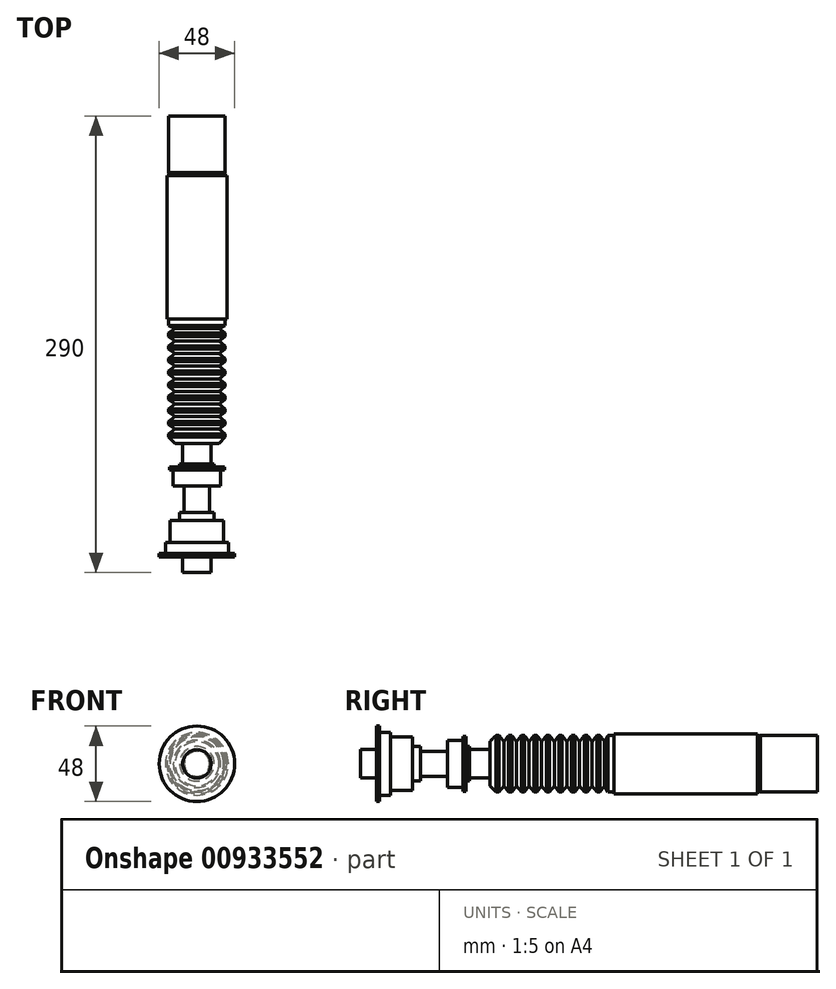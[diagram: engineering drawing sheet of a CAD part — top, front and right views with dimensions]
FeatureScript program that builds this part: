
annotation { "Feature Type Name" : "Feature", "Feature Type Description" : "" }
export const myFeature = defineFeature(function(context is Context, id is Id, definition is map)
    precondition{}
    {
        {
            var Q0;
            Q0=qCreatedBy(makeId("Right.planeOp"),FACE);
            var sketch = newSketch(context, id + "F0", { "sketchPlane" : qUnion([Q0])});
            skLineSegment(sketch, "E0.bottom", {"start": v(0, -9) * mm, "end": v(10, -9) * mm});
            skLineSegment(sketch, "E0.top", {"start": v(0, 9) * mm, "end": v(10, 9) * mm});
            skLineSegment(sketch, "E0.left", {"start": v(0, -9) * mm, "end": v(0, 9) * mm});
            skLineSegment(sketch, "E0.right", {"start": v(10, -9) * mm, "end": v(10, 9) * mm});
            skPoint(sketch, "E0.middle", {"position": v(5, 0) * mm});
            skLineSegment(sketch, "E1.bottom", {"start": v(10, -24) * mm, "end": v(12, -24) * mm});
            skLineSegment(sketch, "E1.top", {"start": v(10, 24) * mm, "end": v(12, 24) * mm});
            skLineSegment(sketch, "E1.left", {"start": v(10, -24) * mm, "end": v(10, 24) * mm});
            skLineSegment(sketch, "E1.right", {"start": v(12, -24) * mm, "end": v(12, 24) * mm});
            skPoint(sketch, "E1.middle", {"position": v(11, 0) * mm});
            skLineSegment(sketch, "E2.bottom", {"start": v(12, -20) * mm, "end": v(19, -20) * mm});
            skLineSegment(sketch, "E2.top", {"start": v(12, 20) * mm, "end": v(19, 20) * mm});
            skLineSegment(sketch, "E2.left", {"start": v(12, -20) * mm, "end": v(12, 20) * mm});
            skLineSegment(sketch, "E2.right", {"start": v(19, -20) * mm, "end": v(19, 20) * mm});
            skPoint(sketch, "E2.middle", {"position": v(15.5, 0) * mm});
            skPoint(sketch, "E2.middle.positionSnap0", {"position": v(12, 0) * mm});
            skPoint(sketch, "E2.centerSnap0", {"position": v(12, 0) * mm});
            skLineSegment(sketch, "E3.bottom", {"start": v(19, -17) * mm, "end": v(33, -17) * mm});
            skLineSegment(sketch, "E3.top", {"start": v(19, 17) * mm, "end": v(33, 17) * mm});
            skLineSegment(sketch, "E3.left", {"start": v(19, -17) * mm, "end": v(19, 17) * mm});
            skLineSegment(sketch, "E3.right", {"start": v(33, -17) * mm, "end": v(33, 17) * mm});
            skPoint(sketch, "E3.middle", {"position": v(26, 0) * mm});
            skLineSegment(sketch, "E4.bottom", {"start": v(33, -11) * mm, "end": v(38, -11) * mm});
            skLineSegment(sketch, "E4.top", {"start": v(33, 11) * mm, "end": v(38, 11) * mm});
            skLineSegment(sketch, "E4.left", {"start": v(33, -11) * mm, "end": v(33, 11) * mm});
            skLineSegment(sketch, "E4.right", {"start": v(38, -11) * mm, "end": v(38, 11) * mm});
            skPoint(sketch, "E4.middle", {"position": v(35.5, 0) * mm});
            skLineSegment(sketch, "E5.bottom", {"start": v(38, -8) * mm, "end": v(55, -8) * mm});
            skLineSegment(sketch, "E5.top", {"start": v(38, 8) * mm, "end": v(55, 8) * mm});
            skLineSegment(sketch, "E5.left", {"start": v(38, -8) * mm, "end": v(38, 8) * mm});
            skLineSegment(sketch, "E5.right", {"start": v(55, -8) * mm, "end": v(55, 8) * mm});
            skPoint(sketch, "E5.middle", {"position": v(46.5, 0) * mm});
            skLineSegment(sketch, "E6.bottom", {"start": v(55, -15) * mm, "end": v(65, -15) * mm});
            skLineSegment(sketch, "E6.top", {"start": v(55, 15) * mm, "end": v(65, 15) * mm});
            skLineSegment(sketch, "E6.left", {"start": v(55, -15) * mm, "end": v(55, 15) * mm});
            skLineSegment(sketch, "E6.right", {"start": v(65, -15) * mm, "end": v(65, 15) * mm});
            skPoint(sketch, "E6.middle", {"position": v(60, 0) * mm});
            skLineSegment(sketch, "E7.bottom", {"start": v(65, -17.5) * mm, "end": v(67, -17.5) * mm});
            skLineSegment(sketch, "E7.top", {"start": v(65, 17.5) * mm, "end": v(67, 17.5) * mm});
            skLineSegment(sketch, "E7.left", {"start": v(65, -17.5) * mm, "end": v(65, 17.5) * mm});
            skLineSegment(sketch, "E7.right", {"start": v(67, -17.5) * mm, "end": v(67, 17.5) * mm});
            skPoint(sketch, "E7.middle", {"position": v(66, 0) * mm});
            skPoint(sketch, "E7.middle.positionSnap0", {"position": v(65, 0) * mm});
            skPoint(sketch, "E7.cornerSnap0", {"position": v(65, 0) * mm});
            skPoint(sketch, "E7.centerSnap0", {"position": v(65, 0) * mm});
            skLineSegment(sketch, "E8.bottom", {"start": v(67, -11) * mm, "end": v(69, -11) * mm});
            skLineSegment(sketch, "E8.top", {"start": v(67, 11) * mm, "end": v(69, 11) * mm});
            skLineSegment(sketch, "E8.left", {"start": v(67, -11) * mm, "end": v(67, 11) * mm});
            skLineSegment(sketch, "E8.right", {"start": v(69, -11) * mm, "end": v(69, 11) * mm});
            skPoint(sketch, "E8.middle", {"position": v(68, 0) * mm});
            skLineSegment(sketch, "E9.bottom", {"start": v(69, -9) * mm, "end": v(82, -9) * mm});
            skLineSegment(sketch, "E9.top", {"start": v(69, 9) * mm, "end": v(82, 9) * mm});
            skLineSegment(sketch, "E9.left", {"start": v(69, -9) * mm, "end": v(69, 9) * mm});
            skLineSegment(sketch, "E9.right", {"start": v(82, -9) * mm, "end": v(82, 9) * mm});
            skPoint(sketch, "E9.middle", {"position": v(75.5, 0) * mm});
            skLineSegment(sketch, "E10", {"start": v(82, 14) * mm, "end": v(82, 0) * mm});
            skLineSegment(sketch, "E11", {"start": v(82, 14) * mm, "end": v(86, 18) * mm});
            skLineSegment(sketch, "E12", {"start": v(86, 18) * mm, "end": v(88, 18) * mm});
            skLineSegment(sketch, "E13", {"start": v(88, 18) * mm, "end": v(91, 14) * mm});
            skLineSegment(sketch, "E14", {"start": v(91, 14) * mm, "end": v(91, 0) * mm});
            skLineSegment(sketch, "E15", {"start": v(91, 0) * mm, "end": v(82, 0) * mm});
            skLineSegment(sketch, "E16", {"start": v(91, 14) * mm, "end": v(94, 18) * mm});
            skLineSegment(sketch, "E17", {"start": v(94, 18) * mm, "end": v(96, 18) * mm});
            skLineSegment(sketch, "E18", {"start": v(96, 18) * mm, "end": v(99, 14) * mm});
            skLineSegment(sketch, "E19", {"start": v(99, 14) * mm, "end": v(99, 0) * mm});
            skLineSegment(sketch, "E20", {"start": v(99, 0) * mm, "end": v(91, 0) * mm});
            skLineSegment(sketch, "E21.1.0.0", {"start": v(107, 14) * mm, "end": v(107, 0) * mm});
            skLineSegment(sketch, "E21.1.0.1", {"start": v(104, 18) * mm, "end": v(107, 14) * mm});
            skLineSegment(sketch, "E21.1.0.2", {"start": v(102, 18) * mm, "end": v(104, 18) * mm});
            skLineSegment(sketch, "E21.1.0.3", {"start": v(99, 14) * mm, "end": v(102, 18) * mm});
            skLineSegment(sketch, "E21.1.0.5", {"start": v(107, 0) * mm, "end": v(99, 0) * mm});
            skLineSegment(sketch, "E21.2.0.0", {"start": v(115, 14) * mm, "end": v(115, 0) * mm});
            skLineSegment(sketch, "E21.2.0.1", {"start": v(112, 18) * mm, "end": v(115, 14) * mm});
            skLineSegment(sketch, "E21.2.0.2", {"start": v(110, 18) * mm, "end": v(112, 18) * mm});
            skLineSegment(sketch, "E21.2.0.3", {"start": v(107, 14) * mm, "end": v(110, 18) * mm});
            skLineSegment(sketch, "E21.2.0.4", {"start": v(107, 14) * mm, "end": v(107, 0) * mm});
            skLineSegment(sketch, "E21.2.0.5", {"start": v(115, 0) * mm, "end": v(107, 0) * mm});
            skLineSegment(sketch, "E21.3.0.0", {"start": v(123, 14) * mm, "end": v(123, 0) * mm});
            skLineSegment(sketch, "E21.3.0.1", {"start": v(120, 18) * mm, "end": v(123, 14) * mm});
            skLineSegment(sketch, "E21.3.0.2", {"start": v(118, 18) * mm, "end": v(120, 18) * mm});
            skLineSegment(sketch, "E21.3.0.3", {"start": v(115, 14) * mm, "end": v(118, 18) * mm});
            skLineSegment(sketch, "E21.3.0.4", {"start": v(115, 14) * mm, "end": v(115, 0) * mm});
            skLineSegment(sketch, "E21.3.0.5", {"start": v(123, 0) * mm, "end": v(115, 0) * mm});
            skLineSegment(sketch, "E21.4.0.0", {"start": v(131, 14) * mm, "end": v(131, 0) * mm});
            skLineSegment(sketch, "E21.4.0.1", {"start": v(128, 18) * mm, "end": v(131, 14) * mm});
            skLineSegment(sketch, "E21.4.0.2", {"start": v(126, 18) * mm, "end": v(128, 18) * mm});
            skLineSegment(sketch, "E21.4.0.3", {"start": v(123, 14) * mm, "end": v(126, 18) * mm});
            skLineSegment(sketch, "E21.4.0.4", {"start": v(123, 14) * mm, "end": v(123, 0) * mm});
            skLineSegment(sketch, "E21.4.0.5", {"start": v(131, 0) * mm, "end": v(123, 0) * mm});
            skLineSegment(sketch, "E21.5.0.0", {"start": v(139, 14) * mm, "end": v(139, 0) * mm});
            skLineSegment(sketch, "E21.5.0.1", {"start": v(136, 18) * mm, "end": v(139, 14) * mm});
            skLineSegment(sketch, "E21.5.0.2", {"start": v(134, 18) * mm, "end": v(136, 18) * mm});
            skLineSegment(sketch, "E21.5.0.3", {"start": v(131, 14) * mm, "end": v(134, 18) * mm});
            skLineSegment(sketch, "E21.5.0.4", {"start": v(131, 14) * mm, "end": v(131, 0) * mm});
            skLineSegment(sketch, "E21.5.0.5", {"start": v(139, 0) * mm, "end": v(131, 0) * mm});
            skLineSegment(sketch, "E21.6.0.0", {"start": v(147, 14) * mm, "end": v(147, 0) * mm});
            skLineSegment(sketch, "E21.6.0.1", {"start": v(144, 18) * mm, "end": v(147, 14) * mm});
            skLineSegment(sketch, "E21.6.0.2", {"start": v(142, 18) * mm, "end": v(144, 18) * mm});
            skLineSegment(sketch, "E21.6.0.3", {"start": v(139, 14) * mm, "end": v(142, 18) * mm});
            skLineSegment(sketch, "E21.6.0.4", {"start": v(139, 14) * mm, "end": v(139, 0) * mm});
            skLineSegment(sketch, "E21.6.0.5", {"start": v(147, 0) * mm, "end": v(139, 0) * mm});
            skLineSegment(sketch, "E21.7.0.0", {"start": v(155, 14) * mm, "end": v(155, 0) * mm});
            skLineSegment(sketch, "E21.7.0.1", {"start": v(152, 18) * mm, "end": v(155, 14) * mm});
            skLineSegment(sketch, "E21.7.0.2", {"start": v(150, 18) * mm, "end": v(152, 18) * mm});
            skLineSegment(sketch, "E21.7.0.3", {"start": v(147, 14) * mm, "end": v(150, 18) * mm});
            skLineSegment(sketch, "E21.7.0.4", {"start": v(147, 14) * mm, "end": v(147, 0) * mm});
            skLineSegment(sketch, "E21.7.0.5", {"start": v(155, 0) * mm, "end": v(147, 0) * mm});
            skLineSegment(sketch, "E21.direction1", {"start": v(99, 0) * mm, "end": v(107, 0) * mm, "construction": true});
            skLineSegment(sketch, "E22", {"start": v(155, 14) * mm, "end": v(157, 18) * mm});
            skLineSegment(sketch, "E23", {"start": v(157, 18) * mm, "end": v(161, 18) * mm});
            skLineSegment(sketch, "E24", {"start": v(161, 18) * mm, "end": v(161, 0) * mm});
            skLineSegment(sketch, "E25", {"start": v(161, 0) * mm, "end": v(155, 0) * mm});
            skLineSegment(sketch, "E26.bottom", {"start": v(161, 19) * mm, "end": v(215, 19) * mm});
            skLineSegment(sketch, "E26.top", {"start": v(161, -19) * mm, "end": v(215, -19) * mm});
            skLineSegment(sketch, "E26.left", {"start": v(161, 19) * mm, "end": v(161, -19) * mm});
            skLineSegment(sketch, "E26.right", {"start": v(215, 19) * mm, "end": v(215, -19) * mm});
            skPoint(sketch, "E26.middle", {"position": v(188, 0) * mm});
            skLineSegment(sketch, "E27.bottom", {"start": v(215, -19) * mm, "end": v(218, -19) * mm});
            skLineSegment(sketch, "E27.top", {"start": v(215, 19) * mm, "end": v(218, 19) * mm});
            skLineSegment(sketch, "E27.left", {"start": v(215, -19) * mm, "end": v(215, 19) * mm});
            skLineSegment(sketch, "E27.right", {"start": v(218, -19) * mm, "end": v(218, 19) * mm});
            skPoint(sketch, "E27.middle", {"position": v(216.5, 0) * mm});
            skPoint(sketch, "E27.middle.positionSnap0", {"position": v(215, 0) * mm});
            skPoint(sketch, "E27.centerSnap0", {"position": v(215, 0) * mm});
            skLineSegment(sketch, "E28.bottom", {"start": v(218, -19) * mm, "end": v(252, -19) * mm});
            skLineSegment(sketch, "E28.top", {"start": v(218, 19) * mm, "end": v(252, 19) * mm});
            skLineSegment(sketch, "E28.right", {"start": v(252, -19) * mm, "end": v(252, 19) * mm});
            skPoint(sketch, "E28.middle", {"position": v(235, 0) * mm});
            skLineSegment(sketch, "E29.bottom", {"start": v(254, -18) * mm, "end": v(262, -18) * mm});
            skLineSegment(sketch, "E29.top", {"start": v(254, 18) * mm, "end": v(262, 18) * mm});
            skLineSegment(sketch, "E29.left", {"start": v(254, -18) * mm, "end": v(254, 18) * mm});
            skLineSegment(sketch, "E29.right", {"start": v(262, -18) * mm, "end": v(262, 18) * mm});
            skPoint(sketch, "E29.middle", {"position": v(258, 0) * mm});
            skPoint(sketch, "E29.middle.positionSnap0", {"position": v(252, 0) * mm});
            skPoint(sketch, "E29.centerSnap0", {"position": v(252, 0) * mm});
            skLineSegment(sketch, "E30", {"start": v(254, 18) * mm, "end": v(252, 17) * mm});
            skLineSegment(sketch, "E31", {"start": v(252, 17) * mm, "end": v(252, -17) * mm});
            skLineSegment(sketch, "E32", {"start": v(252, -17) * mm, "end": v(254, -18) * mm});
            skLineSegment(sketch, "E33.bottom", {"start": v(262, -18) * mm, "end": v(282, -18) * mm});
            skLineSegment(sketch, "E33.top", {"start": v(262, 18) * mm, "end": v(282, 18) * mm});
            skLineSegment(sketch, "E33.right", {"start": v(282, -18) * mm, "end": v(282, 18) * mm});
            skPoint(sketch, "E33.middle", {"position": v(272, 0) * mm});
            skLineSegment(sketch, "E34.bottom", {"start": v(282, -18) * mm, "end": v(290, -18) * mm});
            skLineSegment(sketch, "E34.top", {"start": v(282, 18) * mm, "end": v(290, 18) * mm});
            skLineSegment(sketch, "E34.right", {"start": v(290, -18) * mm, "end": v(290, 18) * mm});
            skPoint(sketch, "E34.middle", {"position": v(286, 0) * mm});
            skLineSegment(sketch, "E35", {"start": v(0, 0) * mm, "end": v(290, 0) * mm});
            skLineSegment(sketch, "E36", {"start": v(0, 0) * mm, "end": v(-2.05, 0) * mm, "construction": true});
            skSolve(sketch);
        }
        {
            var Q0;
            {var subQ0=sQuery(id+"F0.wireOp",EDGE,"E0.top");Q0=makeQuery(id+"F0.imprint","IMPRINT",FACE,{"disambiguationData":[TD([[makeQuery(id+"F0.imprint","IMPRINT",EDGE,{"derivedFrom":subQ0}),-1.0]])]});}
            var Q1;
            {var subQ1=sQuery(id+"F0.wireOp",EDGE,"E1.top");Q1=makeQuery(id+"F0.imprint","IMPRINT",FACE,{"disambiguationData":[TD([[makeQuery(id+"F0.imprint","IMPRINT",EDGE,{"derivedFrom":subQ1}),-1.0]])]});}
            var Q2;
            {var subQ5=sQuery(id+"F0.wireOp",EDGE,"E2.top");Q2=makeQuery(id+"F0.imprint","IMPRINT",FACE,{"disambiguationData":[TD([[makeQuery(id+"F0.imprint","IMPRINT",EDGE,{"derivedFrom":subQ5}),-1.0]])]});}
            var Q3;
            {var subQ5=sQuery(id+"F0.wireOp",EDGE,"E3.top");Q3=makeQuery(id+"F0.imprint","IMPRINT",FACE,{"disambiguationData":[TD([[makeQuery(id+"F0.imprint","IMPRINT",EDGE,{"derivedFrom":subQ5}),-1.0]])]});}
            var Q4;
            {var subQ5=sQuery(id+"F0.wireOp",EDGE,"E4.top");Q4=makeQuery(id+"F0.imprint","IMPRINT",FACE,{"disambiguationData":[TD([[makeQuery(id+"F0.imprint","IMPRINT",EDGE,{"derivedFrom":subQ5}),-1.0]])]});}
            var Q5;
            {var subQ0=sQuery(id+"F0.wireOp",EDGE,"E5.top");Q5=makeQuery(id+"F0.imprint","IMPRINT",FACE,{"disambiguationData":[TD([[makeQuery(id+"F0.imprint","IMPRINT",EDGE,{"derivedFrom":subQ0}),-1.0]])]});}
            var Q6;
            {var subQ1=sQuery(id+"F0.wireOp",EDGE,"E6.top");Q6=makeQuery(id+"F0.imprint","IMPRINT",FACE,{"disambiguationData":[TD([[makeQuery(id+"F0.imprint","IMPRINT",EDGE,{"derivedFrom":subQ1}),-1.0]])]});}
            var Q7;
            {var subQ1=sQuery(id+"F0.wireOp",EDGE,"E7.top");Q7=makeQuery(id+"F0.imprint","IMPRINT",FACE,{"disambiguationData":[TD([[makeQuery(id+"F0.imprint","IMPRINT",EDGE,{"derivedFrom":subQ1}),-1.0]])]});}
            var Q8;
            {var subQ5=sQuery(id+"F0.wireOp",EDGE,"E8.top");Q8=makeQuery(id+"F0.imprint","IMPRINT",FACE,{"disambiguationData":[TD([[makeQuery(id+"F0.imprint","IMPRINT",EDGE,{"derivedFrom":subQ5}),-1.0]])]});}
            var Q9;
            {var subQ0=sQuery(id+"F0.wireOp",EDGE,"E9.top");Q9=makeQuery(id+"F0.imprint","IMPRINT",FACE,{"disambiguationData":[TD([[makeQuery(id+"F0.imprint","IMPRINT",EDGE,{"derivedFrom":subQ0}),-1.0]])]});}
            var Q10;
            {var subQ0=sQuery(id+"F0.wireOp",EDGE,"E11");Q10=makeQuery(id+"F0.imprint","IMPRINT",FACE,{"disambiguationData":[TD([[makeQuery(id+"F0.imprint","IMPRINT",EDGE,{"derivedFrom":subQ0}),-1.0]])]});}
            var Q11;
            {var subQ1=sQuery(id+"F0.wireOp",EDGE,"E14");Q11=makeQuery(id+"F0.imprint","IMPRINT",FACE,{"disambiguationData":[TD([[makeQuery(id+"F0.imprint","IMPRINT",EDGE,{"derivedFrom":subQ1}),1.0]])]});}
            var Q12;
            Q12=makeQuery(id+"F0.imprint","IMPRINT",FACE,{"disambiguationData":[TD([[makeQuery(id+"F0.imprint","IMPRINT",EDGE,{"derivedFrom":sQuery(id+"F0.wireOp",EDGE,"E21.1.0.1")}),-1.0]])]});
            var Q13;
            Q13=makeQuery(id+"F0.imprint","IMPRINT",FACE,{"disambiguationData":[TD([[makeQuery(id+"F0.imprint","IMPRINT",EDGE,{"derivedFrom":sQuery(id+"F0.wireOp",EDGE,"E21.2.0.1")}),-1.0]])]});
            var Q14;
            Q14=makeQuery(id+"F0.imprint","IMPRINT",FACE,{"disambiguationData":[TD([[makeQuery(id+"F0.imprint","IMPRINT",EDGE,{"derivedFrom":sQuery(id+"F0.wireOp",EDGE,"E21.3.0.1")}),-1.0]])]});
            var Q15;
            Q15=makeQuery(id+"F0.imprint","IMPRINT",FACE,{"disambiguationData":[TD([[makeQuery(id+"F0.imprint","IMPRINT",EDGE,{"derivedFrom":sQuery(id+"F0.wireOp",EDGE,"E21.4.0.1")}),-1.0]])]});
            var Q16;
            Q16=makeQuery(id+"F0.imprint","IMPRINT",FACE,{"disambiguationData":[TD([[makeQuery(id+"F0.imprint","IMPRINT",EDGE,{"derivedFrom":sQuery(id+"F0.wireOp",EDGE,"E21.5.0.1")}),-1.0]])]});
            var Q17;
            Q17=makeQuery(id+"F0.imprint","IMPRINT",FACE,{"disambiguationData":[TD([[makeQuery(id+"F0.imprint","IMPRINT",EDGE,{"derivedFrom":sQuery(id+"F0.wireOp",EDGE,"E21.6.0.1")}),-1.0]])]});
            var Q18;
            {var subQ1=sQuery(id+"F0.wireOp",EDGE,"E21.7.0.0");Q18=makeQuery(id+"F0.imprint","IMPRINT",FACE,{"disambiguationData":[TD([[makeQuery(id+"F0.imprint","IMPRINT",EDGE,{"derivedFrom":subQ1}),-1.0]])]});}
            var Q19;
            {var subQ4=sQuery(id+"F0.wireOp",EDGE,"E21.7.0.0");Q19=makeQuery(id+"F0.imprint","IMPRINT",FACE,{"disambiguationData":[TD([[makeQuery(id+"F0.imprint","IMPRINT",EDGE,{"derivedFrom":subQ4}),1.0]])]});}
            var Q20;
            {var subQ1=sQuery(id+"F0.wireOp",EDGE,"E26.bottom");Q20=makeQuery(id+"F0.imprint","IMPRINT",FACE,{"disambiguationData":[TD([[makeQuery(id+"F0.imprint","IMPRINT",EDGE,{"derivedFrom":subQ1}),-1.0]])]});}
            var Q21;
            {var subQ0=sQuery(id+"F0.wireOp",EDGE,"E27.top");Q21=makeQuery(id+"F0.imprint","IMPRINT",FACE,{"disambiguationData":[TD([[makeQuery(id+"F0.imprint","IMPRINT",EDGE,{"derivedFrom":subQ0}),-1.0]])]});}
            var Q22;
            {var subQ1=sQuery(id+"F0.wireOp",EDGE,"E28.top");Q22=makeQuery(id+"F0.imprint","IMPRINT",FACE,{"disambiguationData":[TD([[makeQuery(id+"F0.imprint","IMPRINT",EDGE,{"derivedFrom":subQ1}),-1.0]])]});}
            var Q23;
            {var subQ0=sQuery(id+"F0.wireOp",EDGE,"E30");Q23=makeQuery(id+"F0.imprint","IMPRINT",FACE,{"disambiguationData":[TD([[makeQuery(id+"F0.imprint","IMPRINT",EDGE,{"derivedFrom":subQ0}),1.0]])]});}
            var Q24;
            {var subQ0=sQuery(id+"F0.wireOp",EDGE,"E29.top");Q24=makeQuery(id+"F0.imprint","IMPRINT",FACE,{"disambiguationData":[TD([[makeQuery(id+"F0.imprint","IMPRINT",EDGE,{"derivedFrom":subQ0}),-1.0]])]});}
            var Q25;
            {var subQ0=sQuery(id+"F0.wireOp",EDGE,"E33.top");Q25=makeQuery(id+"F0.imprint","IMPRINT",FACE,{"disambiguationData":[TD([[makeQuery(id+"F0.imprint","IMPRINT",EDGE,{"derivedFrom":subQ0}),-1.0]])]});}
            var Q26;
            {var subQ0=sQuery(id+"F0.wireOp",EDGE,"E34.top");Q26=makeQuery(id+"F0.imprint","IMPRINT",FACE,{"disambiguationData":[TD([[makeQuery(id+"F0.imprint","IMPRINT",EDGE,{"derivedFrom":subQ0}),-1.0]])]});}
            var Q27;
            Q27=sQuery(id+"F0.wireOp",EDGE,"E36");
            revolve(context, id + "F1", {"surfaceOperationType" : NewSurfaceOperationType.NEW, "entities" : qUnion([Q0, Q1, Q2, Q3, Q4, Q5, Q6, Q7, Q8, Q9, Q10, Q11, Q12, Q13, Q14, Q15, Q16, Q17, Q18, Q19, Q20, Q21, Q22, Q23, Q24, Q25, Q26]), "axis" : qUnion([Q27]), "revolveType" : RevolveType.FULL});
        }
    });
